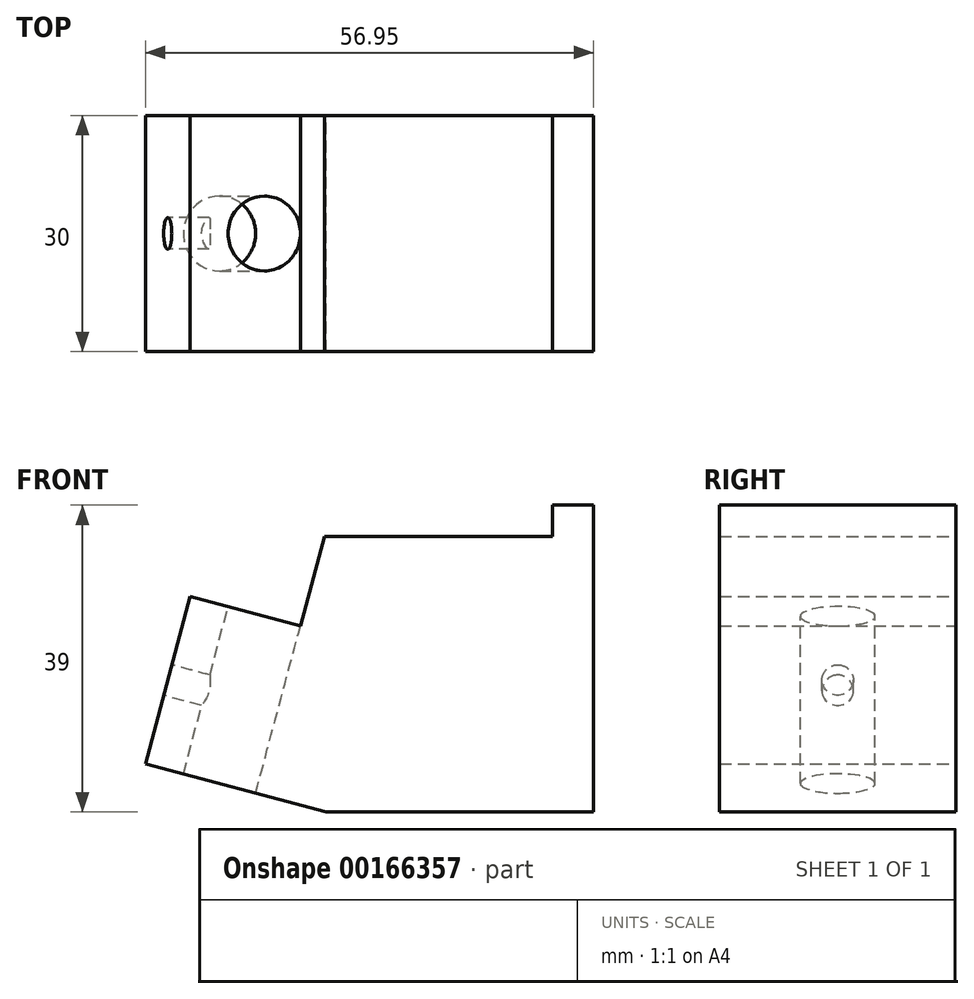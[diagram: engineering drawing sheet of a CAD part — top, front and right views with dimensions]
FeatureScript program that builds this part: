
annotation { "Feature Type Name" : "Feature", "Feature Type Description" : "" }
export const myFeature = defineFeature(function(context is Context, id is Id, definition is map)
    precondition{}
    {
        {
            var Q0;
            Q0=qCreatedBy(makeId("Front.planeOp"),FACE);
            var sketch = newSketch(context, id + "F0", { "sketchPlane" : qUnion([Q0])});
            skLineSegment(sketch, "E0", {"start": v(0, 0) * mm, "end": v(34, 0) * mm});
            skLineSegment(sketch, "E1", {"start": v(34, 0) * mm, "end": v(34, 39) * mm});
            skLineSegment(sketch, "E2", {"start": v(34, 39) * mm, "end": v(28.8, 39) * mm});
            skLineSegment(sketch, "E3", {"start": v(28.8, 39) * mm, "end": v(28.8, 35) * mm});
            skLineSegment(sketch, "E4", {"start": v(28.79, 35) * mm, "end": v(-0.2, 35) * mm});
            skLineSegment(sketch, "E5", {"start": v(-0.21, 35) * mm, "end": v(-3.25, 23.65) * mm});
            skLineSegment(sketch, "E6", {"start": v(-3.25, 23.65) * mm, "end": v(-17.26, 27.4) * mm});
            skLineSegment(sketch, "E7", {"start": v(-17.26, 27.4) * mm, "end": v(-22.95, 6.15) * mm});
            skLineSegment(sketch, "E8", {"start": v(-22.95, 6.15) * mm, "end": v(0, 0) * mm});
            skSolve(sketch);
        }
        {
            var Q0;
            Q0=makeQuery(id+"F0.imprint","IMPRINT",FACE,{"disambiguationData":[TD([[makeQuery(id+"F0.imprint","IMPRINT",EDGE,{"derivedFrom":sQuery(id+"F0.wireOp",EDGE,"E0")}),1.0]])]});
            extrude(context, id + "F1", {"entities" : qUnion([Q0]), "endBound" : BoundingType.SYMMETRIC, "offsetDistance" : 25 * mm, "depth" : 30 * mm});
        }
        {
            var Q0;
            Q0=makeQuery(id+"F1.opExtrude","SWEPT_FACE",FACE,{"disambiguationData":[OSD([sQuery(id+"F0.wireOp",EDGE,"E6")])]});
            var sketch = newSketch(context, id + "F2", { "sketchPlane" : qUnion([Q0])});
            skCircle(sketch, "E9", {"center": v(-14.01, 0) * mm, "radius": 4.75 * mm});
            skLineSegment(sketch, "E10", {"start": v(-14.01, 0) * mm, "end": v(-9.26, 0) * mm, "construction": true});
            skSolve(sketch);
        }
        {
            var Q0;
            Q0=makeQuery(id+"F2.imprint","IMPRINT",FACE,{"disambiguationData":[TD([[makeQuery(id+"F2.imprint","IMPRINT",EDGE,{"derivedFrom":sQuery(id+"F2.wireOp",EDGE,"E9")}),1.0]])]});
            var Q1;
            Q1=sQuery(id+"F2.wireOp",EDGE,"E10");
            var Q2;
            Q2=sQuery(id+"F2.wireOp",EDGE,"E9");
            extrude(context, id + "F3", {"entities" : qUnion([Q0]), "operationType" : NewBodyOperationType.REMOVE, "surfaceEntities" : qUnion([Q1, Q2]), "endBound" : BoundingType.THROUGH_ALL, "oppositeDirection" : true, "depth" : 25 * mm});
        }
        {
            var Q0;
            Q0=makeQuery(id+"F1.opExtrude","SWEPT_FACE",FACE,{"disambiguationData":[OSD([sQuery(id+"F0.wireOp",EDGE,"E7")])]});
            var sketch = newSketch(context, id + "F4", { "sketchPlane" : qUnion([Q0])});
            skLineSegment(sketch, "E11", {"start": v(-15, 22) * mm, "end": v(15, 0) * mm, "construction": true});
            skLineSegment(sketch, "E12", {"start": v(-15, 0) * mm, "end": v(15, 22) * mm, "construction": true});
            skCircle(sketch, "E13", {"center": v(0, 11) * mm, "radius": 2 * mm});
            skSolve(sketch);
        }
        {
            var Q0;
            Q0 = qSketchRegion(id + "F4", true);
            extrude(context, id + "F5", {"entities" : qUnion([Q0]), "operationType" : NewBodyOperationType.REMOVE, "endBound" : BoundingType.UP_TO_NEXT, "oppositeDirection" : true, "depth" : 25 * mm});
        }
    });
